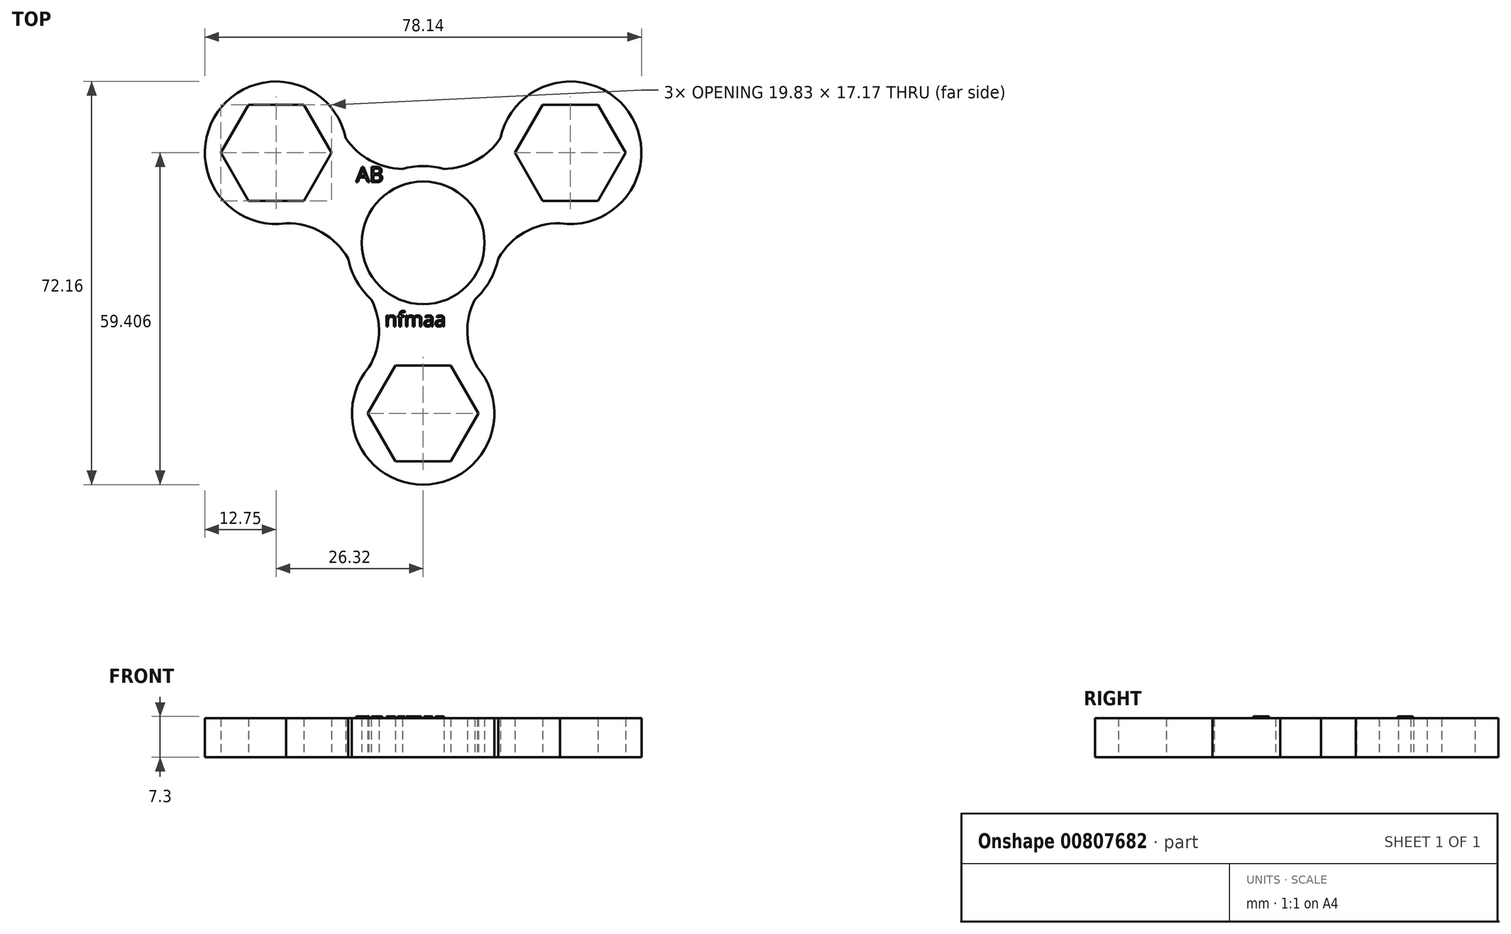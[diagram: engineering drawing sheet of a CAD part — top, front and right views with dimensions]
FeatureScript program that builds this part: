
annotation { "Feature Type Name" : "Feature", "Feature Type Description" : "" }
export const myFeature = defineFeature(function(context is Context, id is Id, definition is map)
    precondition{}
    {
        {
            var Q0;
            Q0=qCreatedBy(makeId("Top.planeOp"),FACE);
            var sketch = newSketch(context, id + "F0", { "sketchPlane" : qUnion([Q0])});
            skCircle(sketch, "E0", {"center": v(0, 0) * mm, "radius": 13.74 * mm});
            skArc(sketch, "E1.MirrorCS", {"start": v(13.84, 18.73) * mm, "mid": v(7.74, 13.96) * mm, "end": v(0, 13.74) * mm});
            skPoint(sketch, "E2", {"position": v(-12.09, -6.52) * mm});
            skPoint(sketch, "E3", {"position": v(12.31, -6.09) * mm});
            skArc(sketch, "E4.MirrorCS", {"start": v(12.09, -6.52) * mm, "mid": v(16.47, 0.75) * mm, "end": v(24.5, 3.5) * mm});
            skArc(sketch, "E5", {"start": v(12.09, -6.52) * mm, "mid": v(8.04, -13.96) * mm, "end": v(9.7, -22.27) * mm});
            skArc(sketch, "E6.MirrorCS", {"start": v(-12.09, -6.52) * mm, "mid": v(-8.04, -13.96) * mm, "end": v(-9.7, -22.27) * mm});
            skCircle(sketch, "E7", {"center": v(0, 0) * mm, "radius": 10.99 * mm});
            skLineSegment(sketch, "E8.0", {"start": v(-4.96, -21.95) * mm, "end": v(4.96, -21.95) * mm});
            skLineSegment(sketch, "E8.1", {"start": v(4.96, -21.95) * mm, "end": v(9.92, -30.54) * mm});
            skLineSegment(sketch, "E8.2", {"start": v(9.92, -30.54) * mm, "end": v(4.96, -39.13) * mm});
            skLineSegment(sketch, "E8.3", {"start": v(4.96, -39.13) * mm, "end": v(-4.96, -39.13) * mm});
            skLineSegment(sketch, "E8.4", {"start": v(-4.96, -39.13) * mm, "end": v(-9.92, -30.54) * mm});
            skLineSegment(sketch, "E8.5", {"start": v(-9.92, -30.54) * mm, "end": v(-4.96, -21.95) * mm});
            skCircle(sketch, "E9", {"center": v(0, -30.54) * mm, "radius": 12.75 * mm});
            skLineSegment(sketch, "E10.0", {"start": v(21.36, 24.7) * mm, "end": v(31.28, 24.7) * mm});
            skLineSegment(sketch, "E10.1", {"start": v(31.28, 24.7) * mm, "end": v(36.24, 16.12) * mm});
            skLineSegment(sketch, "E10.2", {"start": v(36.24, 16.12) * mm, "end": v(31.28, 7.53) * mm});
            skLineSegment(sketch, "E10.3", {"start": v(31.28, 7.53) * mm, "end": v(21.36, 7.53) * mm});
            skLineSegment(sketch, "E10.4", {"start": v(21.36, 7.53) * mm, "end": v(16.4, 16.12) * mm});
            skLineSegment(sketch, "E10.5", {"start": v(16.4, 16.12) * mm, "end": v(21.36, 24.7) * mm});
            skCircle(sketch, "E11", {"center": v(26.32, 16.12) * mm, "radius": 12.75 * mm});
            skLineSegment(sketch, "E12.MirrorCS", {"start": v(-36.24, 16.12) * mm, "end": v(-31.28, 7.53) * mm});
            skLineSegment(sketch, "E13.MirrorCS", {"start": v(-31.28, 7.53) * mm, "end": v(-21.36, 7.53) * mm});
            skLineSegment(sketch, "E14.MirrorCS", {"start": v(-21.36, 7.53) * mm, "end": v(-16.4, 16.12) * mm});
            skLineSegment(sketch, "E15.MirrorCS", {"start": v(-16.4, 16.12) * mm, "end": v(-21.36, 24.7) * mm});
            skLineSegment(sketch, "E16.MirrorCS", {"start": v(-21.36, 24.7) * mm, "end": v(-31.28, 24.7) * mm});
            skLineSegment(sketch, "E17.MirrorCS", {"start": v(-31.28, 24.7) * mm, "end": v(-36.24, 16.12) * mm});
            skCircle(sketch, "E18.MirrorC", {"center": v(-26.32, 16.12) * mm, "radius": 12.75 * mm});
            skArc(sketch, "E19.MirrorCS", {"start": v(-13.84, 18.73) * mm, "mid": v(-7.74, 13.96) * mm, "end": v(0, 13.74) * mm});
            skArc(sketch, "E20.MirrorCS", {"start": v(-12.09, -6.52) * mm, "mid": v(-16.47, 0.75) * mm, "end": v(-24.5, 3.5) * mm});
            skSolve(sketch);
        }
        {
            var Q0;
            Q0=qSketchRegion(id+"F0",true);
            extrude(context, id + "F1", {"entities" : qUnion([Q0]), "depth" : 7 * mm, "offsetDistance" : 25 * mm});
        }
        {
            var Q0;
            Q0=qCreatedBy(makeId("Top.planeOp"),FACE);
            var sketch = newSketch(context, id + "F2", { "sketchPlane" : qUnion([Q0])});
            skText(sketch, "E21", { "text": "nfmaa", "fontName": "OpenSans-Regular.ttf"});
            skText(sketch, "E22", { "text": "AB", "fontName": "OpenSans-Regular.ttf"});
            const initialGuessF2  = {"E21": [-0.00689, -0.01497, 1, 0, 0.00263], "E22": [-0.01203, 0.01084, 1, 0, 0.00276]};
            skSetInitialGuess(sketch, initialGuessF2);
            skSolve(sketch);
        }
        {
            var Q0;
            Q0=qSketchRegion(id+"F2",true);
            extrude(context, id + "F3", {"entities" : qUnion([Q0]), "operationType" : NewBodyOperationType.ADD, "depth" : 7.3 * mm, "offsetDistance" : 25 * mm});
        }
    });
